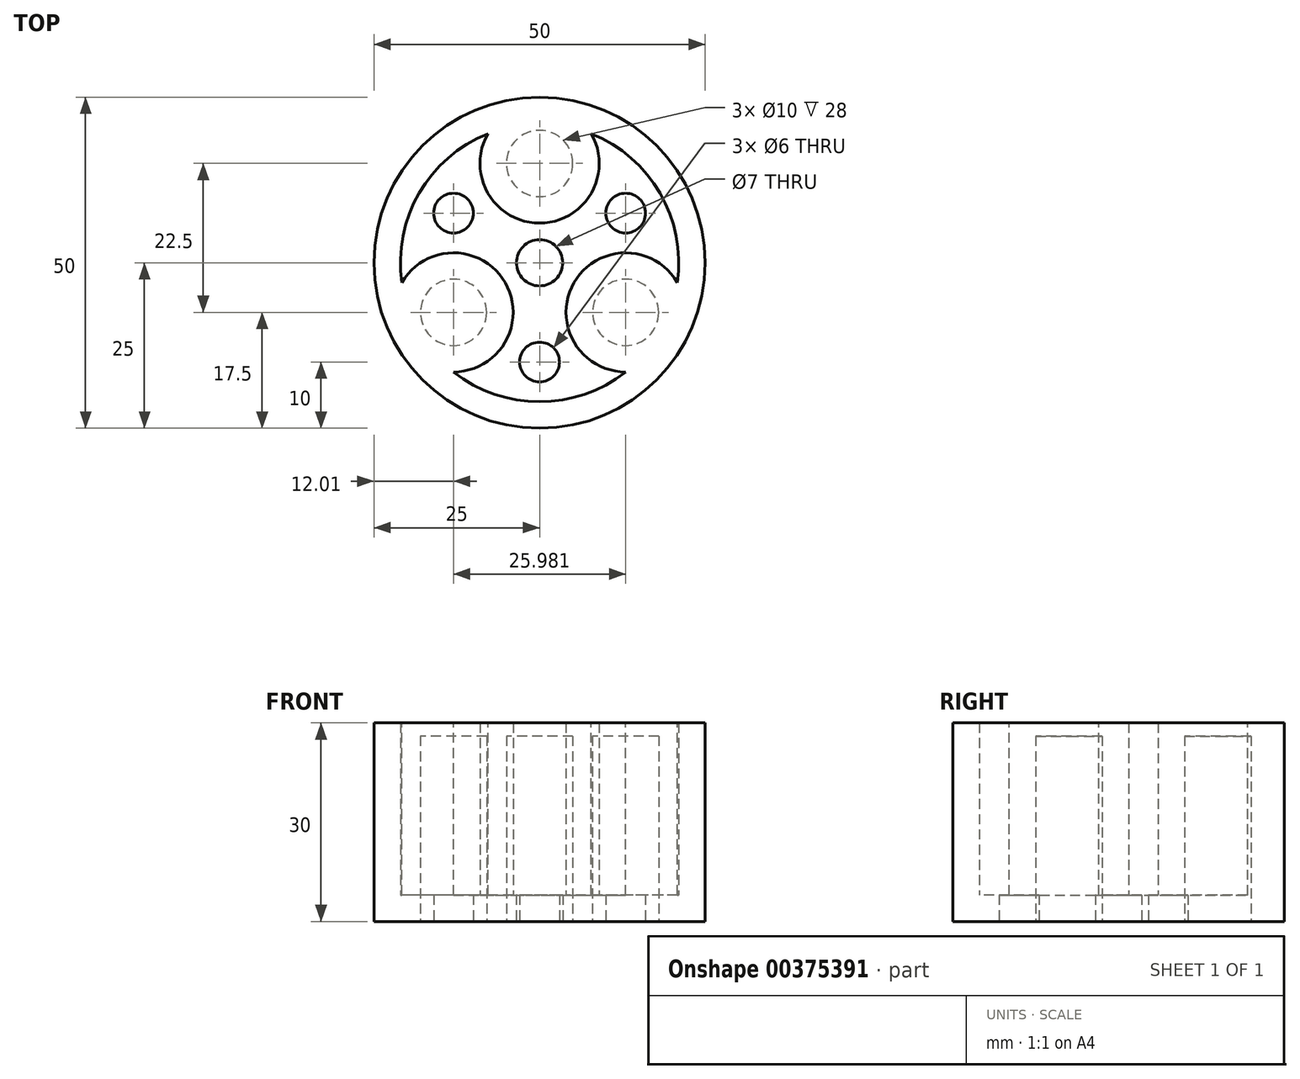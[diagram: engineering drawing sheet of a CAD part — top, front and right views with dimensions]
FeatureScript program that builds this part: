
annotation { "Feature Type Name" : "Feature", "Feature Type Description" : "" }
export const myFeature = defineFeature(function(context is Context, id is Id, definition is map)
    precondition{}
    {
        {
            var Q0;
            Q0=qCreatedBy(makeId("Top.planeOp"),FACE);
            var sketch = newSketch(context, id + "F0", { "sketchPlane" : qUnion([Q0])});
            skCircle(sketch, "E0", {"center": v(0, 0) * mm, "radius": 25 * mm});
            skCircle(sketch, "E1", {"center": v(0, 15) * mm, "radius": 5 * mm});
            skCircle(sketch, "E2", {"center": v(0, 0) * mm, "radius": 3.5 * mm});
            skCircle(sketch, "E3.1.0", {"center": v(-13, -7.5) * mm, "radius": 5 * mm});
            skCircle(sketch, "E3.2.0", {"center": v(13, -7.5) * mm, "radius": 5 * mm});
            skLineSegment(sketch, "E4", {"start": v(0, 15) * mm, "end": v(13, -7.5) * mm, "construction": true});
            skLineSegment(sketch, "E5", {"start": v(0, 0) * mm, "end": v(13, 7.5) * mm, "construction": true});
            skCircle(sketch, "E6", {"center": v(13, 7.5) * mm, "radius": 3 * mm});
            skCircle(sketch, "E7.1.0", {"center": v(-13, 7.5) * mm, "radius": 3 * mm});
            skCircle(sketch, "E7.2.0", {"center": v(0, -15) * mm, "radius": 3 * mm});
            skSolve(sketch);
        }
        {
            var Q0;
            Q0=qSketchRegion(id+"F0",true);
            var Q1;
            Q1=makeQuery(id+"F0.imprint","IMPRINT",FACE,{"disambiguationData":[TD([[makeQuery(id+"F0.imprint","IMPRINT",EDGE,{"derivedFrom":sQuery(id+"F0.wireOp",EDGE,"2f1edcd0-1068-4564-a11f-02244e7b30a9")}),1.0]])]});
            var Q2;
            Q2=makeQuery(id+"F0.imprint","IMPRINT",FACE,{"disambiguationData":[TD([[makeQuery(id+"F0.imprint","IMPRINT",EDGE,{"derivedFrom":sQuery(id+"F0.wireOp",EDGE,"E2")}),1.0]])]});
            var Q3;
            Q3=makeQuery(id+"F0.imprint","IMPRINT",FACE,{"disambiguationData":[TD([[makeQuery(id+"F0.imprint","IMPRINT",EDGE,{"derivedFrom":sQuery(id+"F0.wireOp",EDGE,"E7.1.0")}),1.0]])]});
            var Q4;
            Q4=makeQuery(id+"F0.imprint","IMPRINT",FACE,{"disambiguationData":[TD([[makeQuery(id+"F0.imprint","IMPRINT",EDGE,{"derivedFrom":sQuery(id+"F0.wireOp",EDGE,"E6")}),1.0]])]});
            var Q5;
            Q5=makeQuery(id+"F0.imprint","IMPRINT",FACE,{"disambiguationData":[TD([[makeQuery(id+"F0.imprint","IMPRINT",EDGE,{"derivedFrom":sQuery(id+"F0.wireOp",EDGE,"E7.2.0")}),1.0]])]});
            extrude(context, id + "F1", {"entities" : qUnion([Q0, Q1, Q2, Q3, Q4, Q5]), "depth" : 28 * mm});
        }
        {
            var Q0;
            Q0=makeQuery(id+"F1.opExtrude","CAP_FACE",FACE,{"disambiguationData":[OSD([sQuery(id+"F0.wireOp",EDGE,"E0"),sQuery(id+"F0.wireOp",EDGE,"E1"),sQuery(id+"F0.wireOp",EDGE,"15a5e05c-d03d-43cd-ad20-06248263a0d0.1.0"),sQuery(id+"F0.wireOp",EDGE,"15a5e05c-d03d-43cd-ad20-06248263a0d0.2.0"),sQuery(id+"F0.wireOp",EDGE,"15a5e05c-d03d-43cd-ad20-06248263a0d0.3.0")])],"isStart":false});
            shell(context, id + "F2", {"entities" : qUnion([Q0]), "thickness" : 4 * mm});
        }
        {
            var Q0;
            Q0=makeQuery(id+"F0.imprint","IMPRINT",FACE,{"disambiguationData":[TD([[makeQuery(id+"F0.imprint","IMPRINT",EDGE,{"derivedFrom":sQuery(id+"F0.wireOp",EDGE,"E7.1.0")}),1.0]])]});
            var Q1;
            Q1=makeQuery(id+"F0.imprint","IMPRINT",FACE,{"disambiguationData":[TD([[makeQuery(id+"F0.imprint","IMPRINT",EDGE,{"derivedFrom":sQuery(id+"F0.wireOp",EDGE,"E2")}),1.0]])]});
            var Q2;
            Q2=makeQuery(id+"F0.imprint","IMPRINT",FACE,{"disambiguationData":[TD([[makeQuery(id+"F0.imprint","IMPRINT",EDGE,{"derivedFrom":sQuery(id+"F0.wireOp",EDGE,"E6")}),1.0]])]});
            var Q3;
            Q3=makeQuery(id+"F0.imprint","IMPRINT",FACE,{"disambiguationData":[TD([[makeQuery(id+"F0.imprint","IMPRINT",EDGE,{"derivedFrom":sQuery(id+"F0.wireOp",EDGE,"E7.2.0")}),1.0]])]});
            extrude(context, id + "F3", {"entities" : qUnion([Q0, Q1, Q2, Q3]), "operationType" : NewBodyOperationType.REMOVE, "depth" : 25 * mm});
        }
        {
            var Q0;
            Q0=makeQuery(id+"F1.opExtrude","CAP_FACE",FACE,{"disambiguationData":[OSD([sQuery(id+"F0.wireOp",EDGE,"E0"),sQuery(id+"F0.wireOp",EDGE,"E1"),sQuery(id+"F0.wireOp",EDGE,"E3.1.0"),sQuery(id+"F0.wireOp",EDGE,"E3.2.0")])],"isStart":false});
            var sketch = newSketch(context, id + "F4", { "sketchPlane" : qUnion([Q0])});
            skCircle(sketch, "E8.0.0", {"center": v(0, 0) * mm, "radius": 25 * mm});
            skArc(sketch, "E9.0", {"start": v(-7.8, 19.5) * mm, "mid": v(-18.19, 10.5) * mm, "end": v(-20.78, -3) * mm});
            skArc(sketch, "E10.0", {"start": v(-7.8, 19.5) * mm, "mid": v(0, 6) * mm, "end": v(7.8, 19.5) * mm});
            skArc(sketch, "E11.0", {"start": v(20.78, -3) * mm, "mid": v(5.2, -3) * mm, "end": v(13, -16.5) * mm});
            skArc(sketch, "E12.0", {"start": v(20.78, -3) * mm, "mid": v(18.19, 10.5) * mm, "end": v(7.8, 19.5) * mm});
            skArc(sketch, "E13.0", {"start": v(-13, -16.5) * mm, "mid": v(0, -21) * mm, "end": v(13, -16.5) * mm});
            skArc(sketch, "E14.0", {"start": v(-13, -16.5) * mm, "mid": v(-5.2, -3) * mm, "end": v(-20.78, -3) * mm});
            skSolve(sketch);
        }
        {
            var Q0;
            Q0=qSketchRegion(id+"F4",true);
            extrude(context, id + "F5", {"entities" : qUnion([Q0]), "operationType" : NewBodyOperationType.ADD, "depth" : 2 * mm, "offsetDistance" : 25 * mm});
        }
    });
